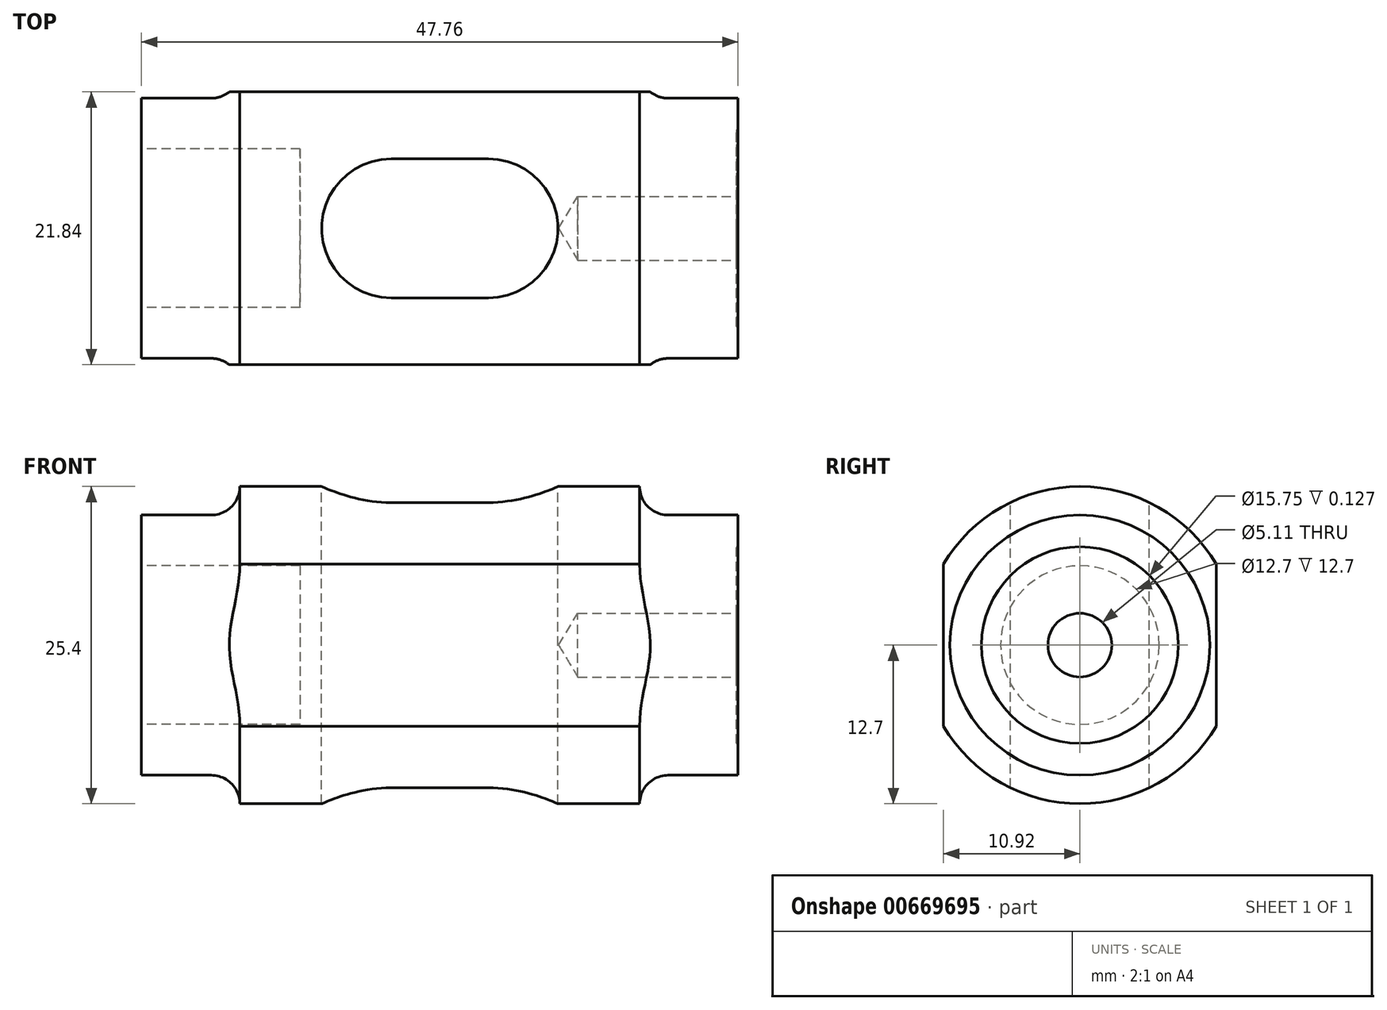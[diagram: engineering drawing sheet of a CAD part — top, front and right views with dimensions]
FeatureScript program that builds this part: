
annotation { "Feature Type Name" : "Feature", "Feature Type Description" : "" }
export const myFeature = defineFeature(function(context is Context, id is Id, definition is map)
    precondition{}
    {
        {
            var Q0;
            Q0=qCreatedBy(makeId("Top.planeOp"),FACE);
            var sketch = newSketch(context, id + "F0", { "sketchPlane" : qUnion([Q0])});
            skLineSegment(sketch, "E0.bottom", {"start": v(-16, 12.7) * mm, "end": v(16, 12.7) * mm});
            skLineSegment(sketch, "E0.top", {"start": v(-23.88, 0) * mm, "end": v(23.88, 0) * mm});
            skLineSegment(sketch, "E0.left", {"start": v(-23.88, 10.41) * mm, "end": v(-23.88, 0) * mm});
            skLineSegment(sketch, "E0.right", {"start": v(23.88, 10.41) * mm, "end": v(23.88, 0) * mm});
            skLineSegment(sketch, "E1", {"start": v(-23.88, 10.41) * mm, "end": v(-18.29, 10.41) * mm});
            skLineSegment(sketch, "E2", {"start": v(-16, 12.7) * mm, "end": v(-16, 12.7) * mm});
            skLineSegment(sketch, "E3", {"start": v(0, 0) * mm, "end": v(0, 15.25) * mm, "construction": true});
            skPoint(sketch, "E3.endSnap0", {"position": v(0, 12.7) * mm});
            skPoint(sketch, "E4.visualSharp", {"position": v(-16, 10.41) * mm});
            skArc(sketch, "E4.filletArc", {"start": v(-18.29, 10.41) * mm, "mid": v(-16.67, 11.08) * mm, "end": v(-16, 12.7) * mm});
            skArc(sketch, "E5.MirrorCS", {"start": v(18.29, 10.41) * mm, "mid": v(16.67, 11.08) * mm, "end": v(16, 12.7) * mm});
            skLineSegment(sketch, "E6.MirrorCS", {"start": v(23.88, 10.41) * mm, "end": v(18.29, 10.41) * mm});
            skPoint(sketch, "E7.orphan", {"position": v(-23.88, 12.7) * mm});
            skPoint(sketch, "E8.orphan", {"position": v(23.88, 12.7) * mm});
            skLineSegment(sketch, "E9", {"start": v(-25.7, 0) * mm, "end": v(25.82, 0) * mm, "construction": true});
            skSolve(sketch);
        }
        {
            var Q0;
            Q0=qSketchRegion(id+"F0",true);
            var Q1;
            Q1=sQuery(id+"F0.wireOp",EDGE,"E9");
            revolve(context, id + "F1", {"entities" : qUnion([Q0]), "axis" : qUnion([Q1]), "revolveType" : RevolveType.FULL});
        }
        {
            var Q0;
            Q0=qCreatedBy(makeId("Top.planeOp"),FACE);
            var sketch = newSketch(context, id + "F2", { "sketchPlane" : qUnion([Q0])});
            skLineSegment(sketch, "E10", {"start": v(-23.88, 0) * mm, "end": v(23.88, 0) * mm, "construction": true});
            skLineSegment(sketch, "E11.bottom", {"start": v(-18.85, 16.78) * mm, "end": v(19.24, 16.78) * mm});
            skLineSegment(sketch, "E11.top", {"start": v(-18.85, 10.92) * mm, "end": v(19.24, 10.92) * mm});
            skLineSegment(sketch, "E11.left", {"start": v(-18.85, 16.78) * mm, "end": v(-18.85, 10.92) * mm});
            skLineSegment(sketch, "E11.right", {"start": v(19.24, 16.78) * mm, "end": v(19.24, 10.92) * mm});
            skLineSegment(sketch, "E12.MirrorCS", {"start": v(19.24, -16.78) * mm, "end": v(19.24, -10.92) * mm});
            skLineSegment(sketch, "E13.MirrorCS", {"start": v(-18.85, -16.78) * mm, "end": v(-18.85, -10.92) * mm});
            skLineSegment(sketch, "E14.MirrorCS", {"start": v(-18.85, -10.92) * mm, "end": v(19.24, -10.92) * mm});
            skLineSegment(sketch, "E15.MirrorCS", {"start": v(-18.85, -16.78) * mm, "end": v(19.24, -16.78) * mm});
            skLineSegment(sketch, "E16.bottom", {"start": v(3.9, 5.56) * mm, "end": v(-3.9, 5.56) * mm});
            skLineSegment(sketch, "E16.top", {"start": v(3.9, -5.56) * mm, "end": v(-3.9, -5.56) * mm});
            skPoint(sketch, "E16.middle", {"position": v(0, 0) * mm});
            skPoint(sketch, "E17.visualSharp", {"position": v(-9.46, 5.56) * mm});
            skArc(sketch, "E17.filletArc", {"start": v(-3.9, 5.56) * mm, "mid": v(-7.83, 3.93) * mm, "end": v(-9.46, 0) * mm});
            skPoint(sketch, "E18.visualSharp", {"position": v(-9.46, -5.56) * mm});
            skArc(sketch, "E18.filletArc", {"start": v(-9.46, 0) * mm, "mid": v(-7.83, -3.93) * mm, "end": v(-3.9, -5.56) * mm});
            skPoint(sketch, "E19.visualSharp", {"position": v(9.46, 5.56) * mm});
            skArc(sketch, "E19.filletArc", {"start": v(9.46, 0) * mm, "mid": v(7.83, 3.93) * mm, "end": v(3.9, 5.56) * mm});
            skPoint(sketch, "E20.visualSharp", {"position": v(9.46, -5.56) * mm});
            skArc(sketch, "E20.filletArc", {"start": v(3.9, -5.56) * mm, "mid": v(7.83, -3.93) * mm, "end": v(9.46, 0) * mm});
            skSolve(sketch);
        }
        {
            var Q0;
            Q0=qSketchRegion(id+"F2",true);
            extrude(context, id + "F3", {"entities" : qUnion([Q0]), "operationType" : NewBodyOperationType.REMOVE, "oppositeDirection" : true, "depth" : 25.4 * mm, "offsetDistance" : 25.4 * mm, "hasSecondDirection" : true, "secondDirectionOppositeDirection" : false, "secondDirectionDepth" : 25.4 * mm, "symmetric" : true});
        }
        {
            var Q0;
            Q0=makeQuery(id+"F1.opRevolve","SWEPT_FACE",FACE,{"disambiguationData":[OSD([sQuery(id+"F0.wireOp",EDGE,"E0.right")])]});
            var sketch = newSketch(context, id + "F4", { "sketchPlane" : qUnion([Q0])});
            skCircle(sketch, "E21", {"center": v(0, 0) * mm, "radius": 7.87 * mm});
            skSolve(sketch);
        }
        {
            var Q0;
            Q0=qSketchRegion(id+"F4",true);
            extrude(context, id + "F5", {"entities" : qUnion([Q0]), "operationType" : NewBodyOperationType.REMOVE, "oppositeDirection" : true, "depth" : 0.13 * mm, "offsetDistance" : 25.4 * mm});
        }
        {
            var Q0;
            Q0=makeQuery(id+"F5.boolean.opBoolean","COPY",FACE,{"derivedFrom":makeQuery(id+"F5.opExtrude","CAP_FACE",FACE,{"disambiguationData":[OSD([sQuery(id+"F4.wireOp",EDGE,"E21")])],"isStart":false})});
            var sketch = newSketch(context, id + "F6", { "sketchPlane" : qUnion([Q0])});
            skPoint(sketch, "E22", {"position": v(0, 0) * mm});
            skSolve(sketch);
        }
        {
            var Q0;
            Q0=sQuery(id+"F6.wireOp",VERTEX,"E22");
            var Q1;
            Q1=makeQuery(id+"F1.opRevolve","SWEPT_BODY",BODY,{"disambiguationData":[OSD([sQuery(id+"F0.wireOp",EDGE,"E0.bottom"),sQuery(id+"F0.wireOp",EDGE,"E0.top"),sQuery(id+"F0.wireOp",EDGE,"E0.left"),sQuery(id+"F0.wireOp",EDGE,"E0.right"),sQuery(id+"F0.wireOp",EDGE,"E1"),sQuery(id+"F0.wireOp",EDGE,"E4.filletArc"),sQuery(id+"F0.wireOp",EDGE,"E5.MirrorCS"),sQuery(id+"F0.wireOp",EDGE,"E6.MirrorCS")])]});
            hole(context, id + "F7", {"style" : HoleStyle.SIMPLE, "endStyle" : HoleEndStyle.BLIND, "standardTappedOrClearance" : lookupTablePath({ "standard" : "ANSI", "engagement" : "75%", "pitch" : "20 tpi", "size" : "1/4", "type" : "Tapped" }), "standardBlindInLast" : lookupTablePath({ "standard" : "ANSI", "engagement" : "75%", "pitch" : "20 tpi", "size" : "1/4", "type" : "Tapped" }), "holeDiameter" : 5.1 * mm, "majorDiameter" : 6.35 * mm, "showTappedDepth" : true, "holeDepth" : 12.7 * mm, "isTappedThrough" : true, "tappedDepth" : 8.9 * mm, "tapClearance" : 3, "locations" : qUnion([Q0]), "scope" : qUnion([Q1])});
        }
        {
            var Q0;
            Q0=makeQuery(id+"F1.opRevolve","SWEPT_FACE",FACE,{"disambiguationData":[OSD([sQuery(id+"F0.wireOp",EDGE,"E0.left")])]});
            var sketch = newSketch(context, id + "F8", { "sketchPlane" : qUnion([Q0])});
            skCircle(sketch, "E23", {"center": v(0, 0) * mm, "radius": 6.35 * mm});
            skSolve(sketch);
        }
        {
            var Q0;
            Q0=qSketchRegion(id+"F8",true);
            extrude(context, id + "F9", {"entities" : qUnion([Q0]), "operationType" : NewBodyOperationType.REMOVE, "oppositeDirection" : true, "depth" : 12.7 * mm, "offsetDistance" : 25.4 * mm});
        }
    });
